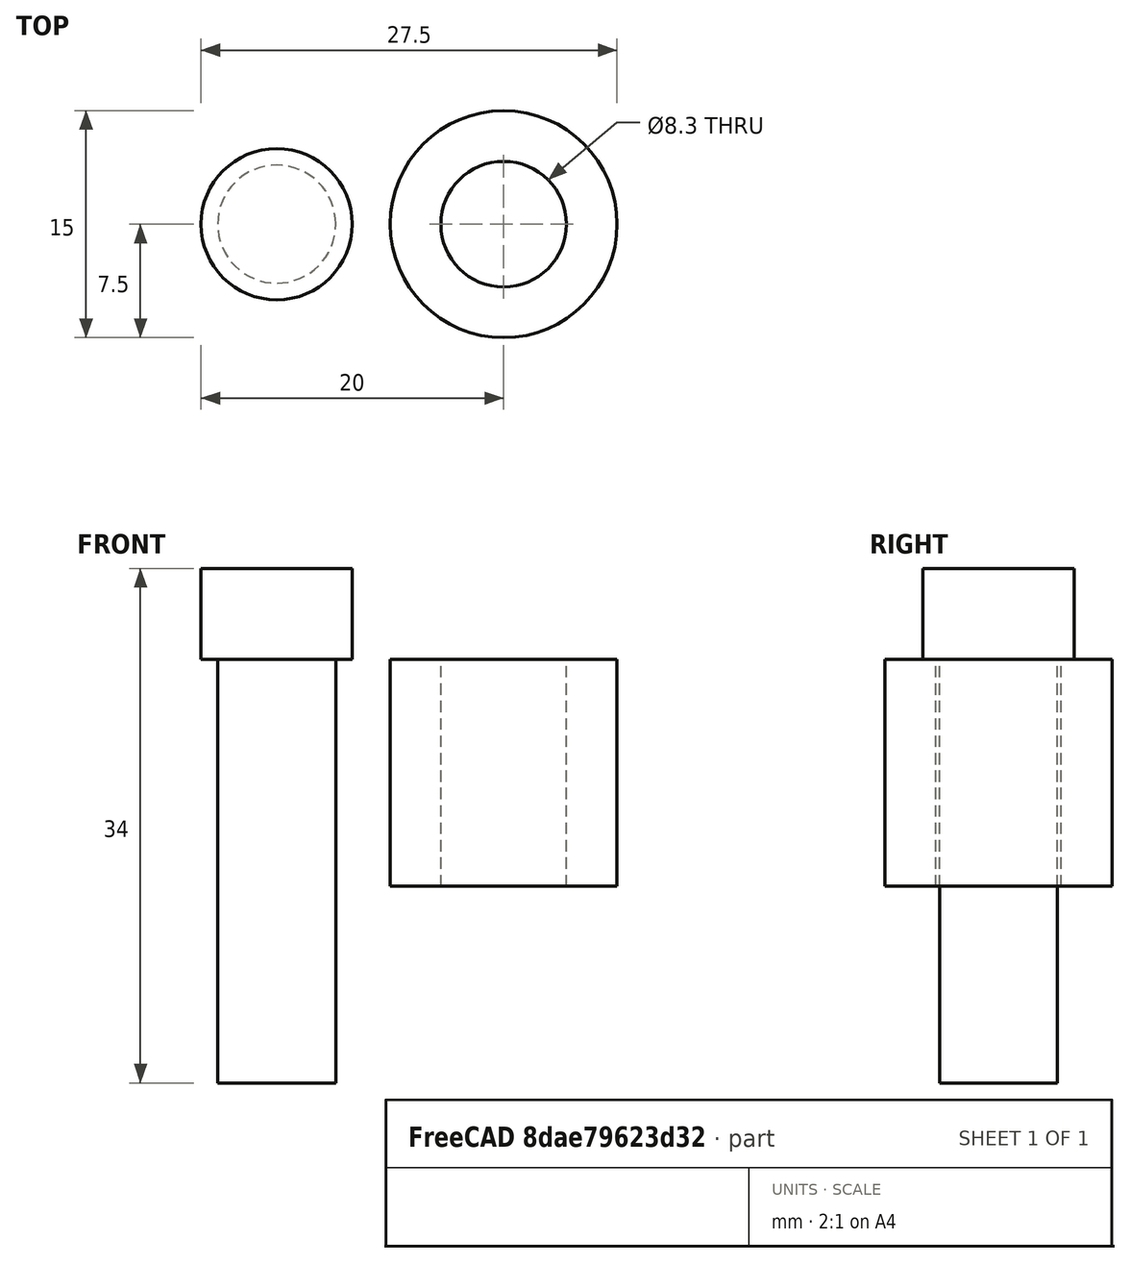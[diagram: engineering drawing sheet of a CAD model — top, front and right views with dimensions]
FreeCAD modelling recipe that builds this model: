
FCSTD DOCUMENT  (FreeCAD 0.19R24291 (Git))
Label: vástago dos partes
License: All rights reserved
LicenseURL: http://en.wikipedia.org/wiki/All_rights_reserved
objects: Part::FeaturePython×2, Part::Cylinder×1, Part::MultiFuse×1
note: 4 computed .brp shape members not serialized (recipe doc carries the construction recipe); baked Part::Feature solids carry a one-line shape summary decoded from their .brp

FEATURE [Part::Cylinder] Cylinder  label="Cilindro"
  Angle = 360
  AttacherType = Attacher::AttachEngine3D
  Height = 34
  Placement = pos=(0,0,-5) rot=(0,0,1;0rad)
  Radius = 3.9
FEATURE [Part::FeaturePython] Tube  # WARN: FeaturePython — macro-defined, semantics opaque (R4)
  AttacherType = Attacher::AttachEngine3D
  Height = 15
  InnerRadius = 4.15
  OuterRadius = 7.5
  Placement = pos=(15,0,8) rot=(0,0,1;0rad)
FEATURE [Part::FeaturePython] Tube001  # WARN: FeaturePython — macro-defined, semantics opaque (R4)
  AttacherType = Attacher::AttachEngine3D
  Height = 6
  InnerRadius = 3.9
  OuterRadius = 5
  Placement = pos=(0,0,23) rot=(0,0,1;0rad)
FEATURE [Part::MultiFuse] Fusion
  Shapes = -> [Cylinder,Tube001]
